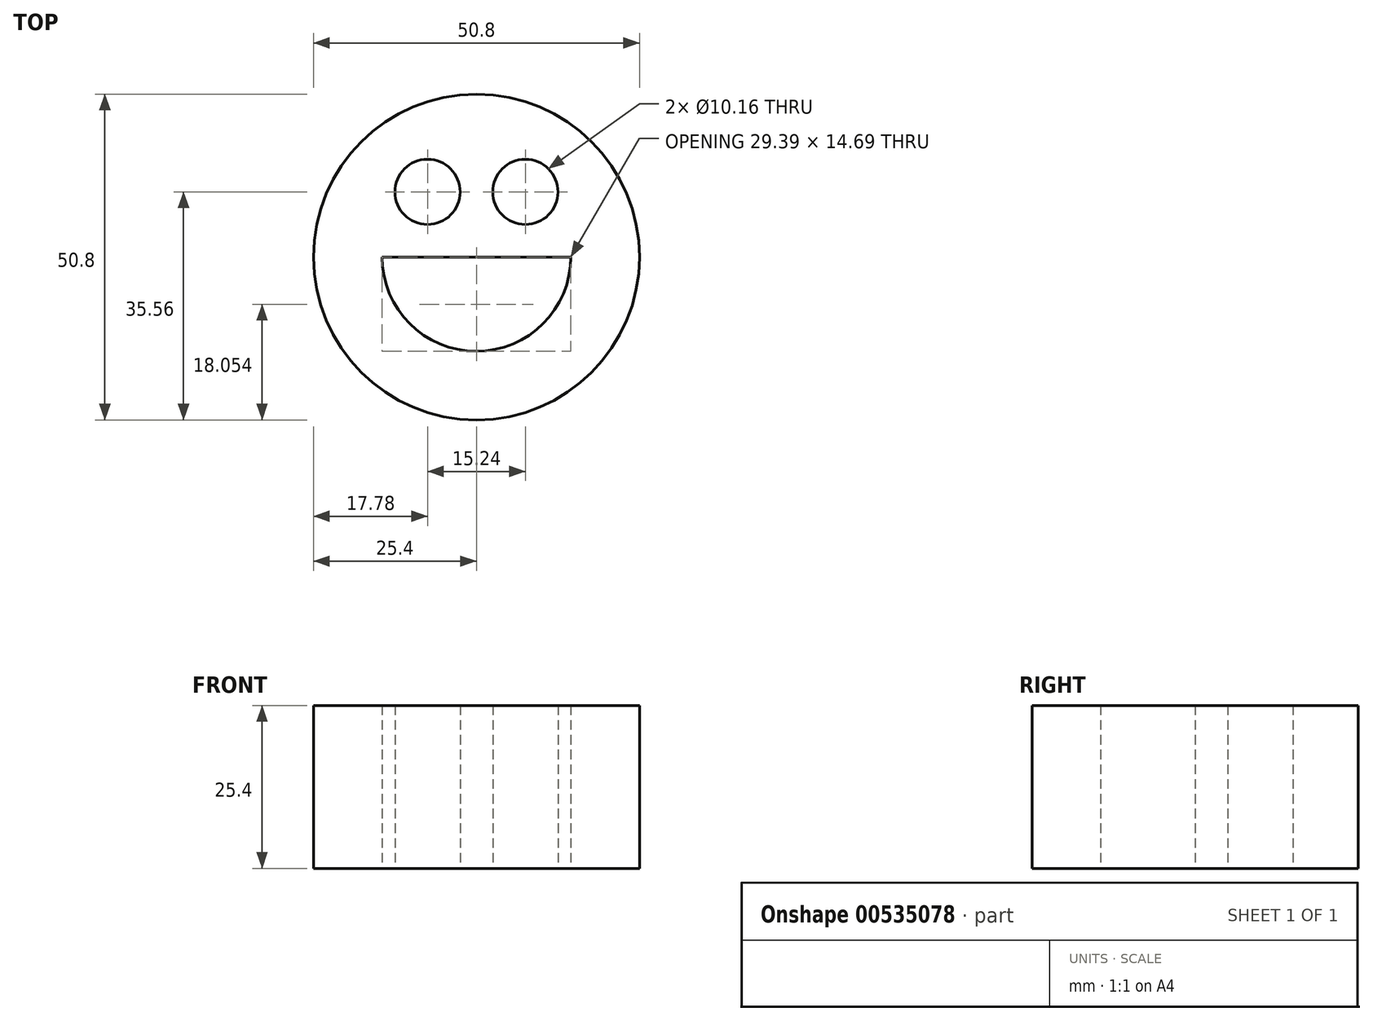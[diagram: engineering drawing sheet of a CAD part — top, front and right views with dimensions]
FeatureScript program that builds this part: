
annotation { "Feature Type Name" : "Feature", "Feature Type Description" : "" }
export const myFeature = defineFeature(function(context is Context, id is Id, definition is map)
    precondition{}
    {
        {
            var Q0;
            Q0=qCreatedBy(makeId("Top.planeOp"),FACE);
            var sketch = newSketch(context, id + "F0", { "sketchPlane" : qUnion([Q0])});
            skCircle(sketch, "E0", {"center": v(0, 0) * mm, "radius": 25.4 * mm});
            skCircle(sketch, "E1", {"center": v(-7.62, 10.16) * mm, "radius": 5.08 * mm});
            skCircle(sketch, "E2", {"center": v(7.62, 10.16) * mm, "radius": 5.08 * mm});
            skArc(sketch, "E3", {"start": v(-14.7, 0) * mm, "mid": v(0, -14.7) * mm, "end": v(14.7, 0) * mm});
            skLineSegment(sketch, "E4", {"start": v(-14.7, 0) * mm, "end": v(14.7, 0) * mm});
            skSolve(sketch);
        }
        {
            var Q0;
            Q0 = qSketchRegion(id + "F0", true);
            extrude(context, id + "F1", {"entities" : qUnion([Q0]), "depth" : 25.4 * mm, "offsetDistance" : 25.4 * mm});
        }
    });
